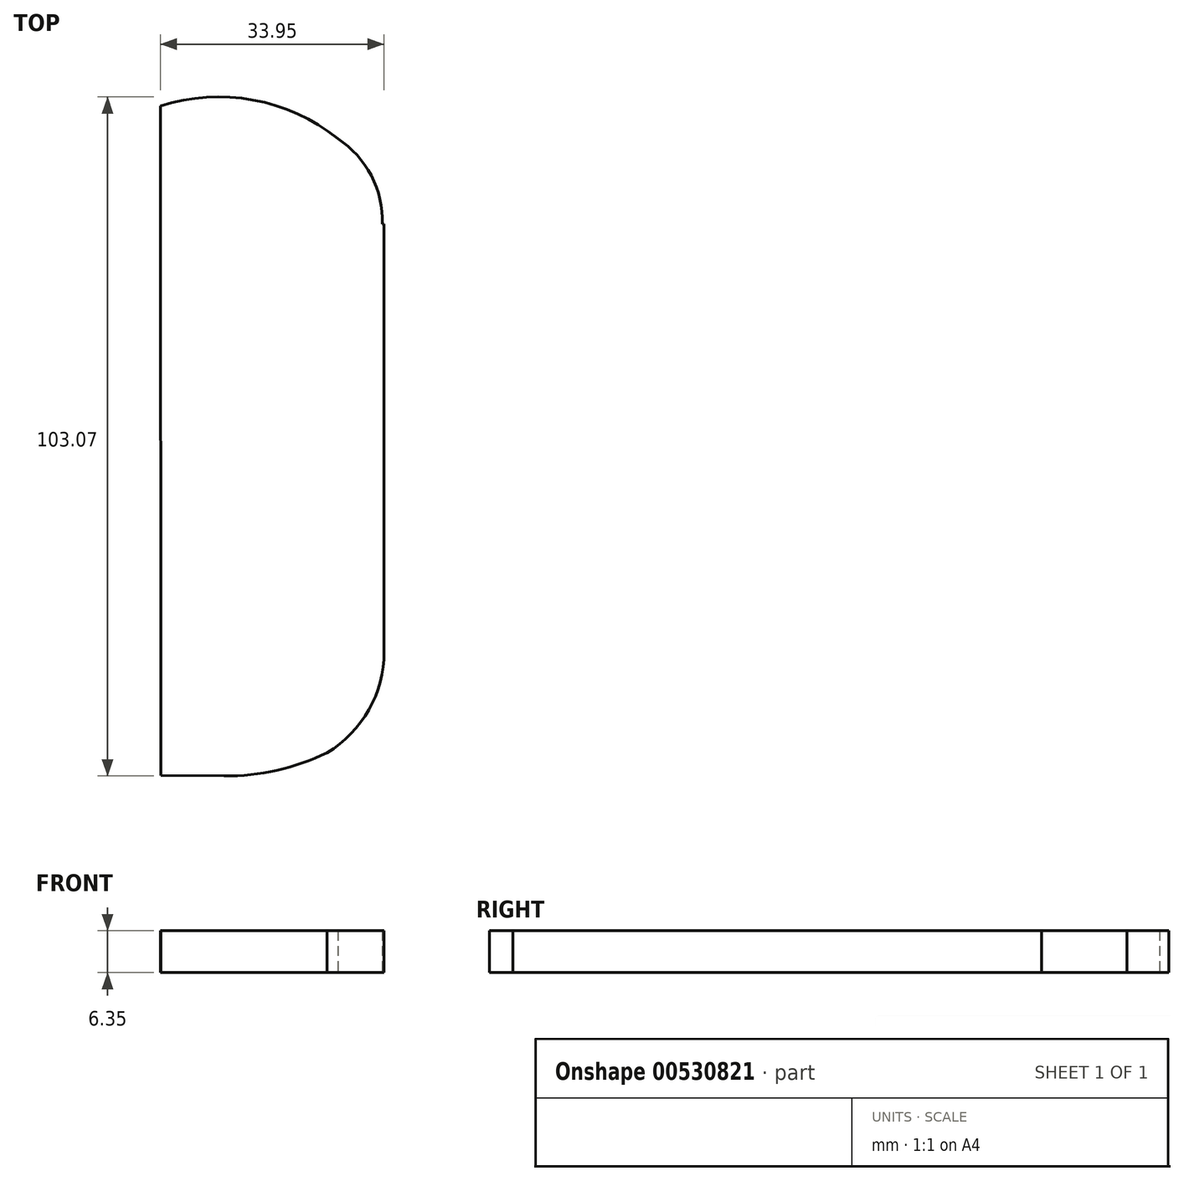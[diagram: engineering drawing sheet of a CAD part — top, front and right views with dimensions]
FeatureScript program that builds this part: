
annotation { "Feature Type Name" : "Feature", "Feature Type Description" : "" }
export const myFeature = defineFeature(function(context is Context, id is Id, definition is map)
    precondition{}
    {
        {
            var Q0;
            Q0=qCreatedBy(makeId("Top.planeOp"),FACE);
            var sketch = newSketch(context, id + "F0", { "sketchPlane" : qUnion([Q0])});
            skArc(sketch, "E0", {"start": v(87.17, 52.67) * mm, "mid": v(74.33, 58.55) * mm, "end": v(60.24, 57.62) * mm});
            skArc(sketch, "E1", {"start": v(93.95, 39.7) * mm, "mid": v(92.26, 47.07) * mm, "end": v(87.17, 52.67) * mm});
            skLineSegment(sketch, "E2", {"start": v(94.2, 39.7) * mm, "end": v(94.2, -25.22) * mm});
            skArc(sketch, "E3", {"start": v(85.56, -40.51) * mm, "mid": v(91.89, -34) * mm, "end": v(94.2, -25.22) * mm});
            skArc(sketch, "E4", {"start": v(69.91, -44.05) * mm, "mid": v(77.94, -43.18) * mm, "end": v(85.56, -40.51) * mm});
            skLineSegment(sketch, "E5", {"start": v(69.91, -44.05) * mm, "end": v(60.35, -43.98) * mm});
            skLineSegment(sketch, "E6", {"start": v(60.35, -43.98) * mm, "end": v(60.24, 57.62) * mm});
            skLineSegment(sketch, "E7", {"start": v(93.95, 39.7) * mm, "end": v(94.2, 39.7) * mm});
            skSolve(sketch);
        }
        {
            var Q0;
            Q0=makeQuery(id+"F0.imprint","IMPRINT",FACE,{"disambiguationData":[TD([[makeQuery(id+"F0.imprint","IMPRINT",EDGE,{"derivedFrom":sQuery(id+"F0.wireOp",EDGE,"E0")}),1.0]])]});
            extrude(context, id + "F1", {"entities" : qUnion([Q0]), "depth" : 6.35 * mm, "offsetDistance" : 25.4 * mm});
        }
    });
